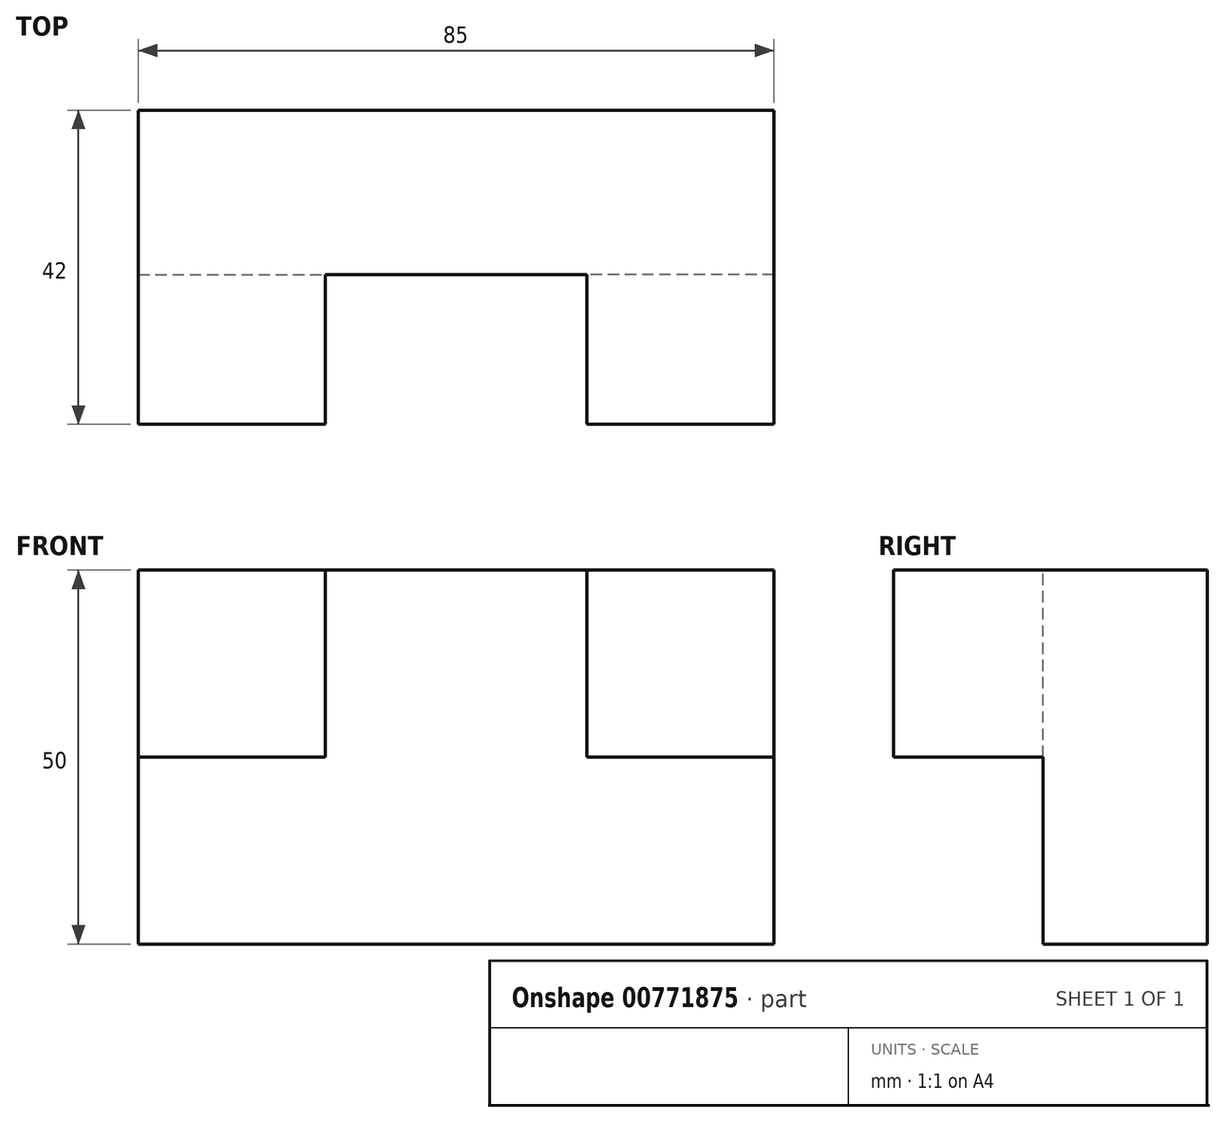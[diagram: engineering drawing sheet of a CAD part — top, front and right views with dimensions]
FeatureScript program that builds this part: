
annotation { "Feature Type Name" : "Feature", "Feature Type Description" : "" }
export const myFeature = defineFeature(function(context is Context, id is Id, definition is map)
    precondition{}
    {
        {
            var Q0;
            Q0=qCreatedBy(makeId("Front.planeOp"),FACE);
            var sketch = newSketch(context, id + "F0", { "sketchPlane" : qUnion([Q0])});
            skLineSegment(sketch, "E0", {"start": v(0, 0) * mm, "end": v(0, 50) * mm});
            skLineSegment(sketch, "E1", {"start": v(0, 50) * mm, "end": v(85, 50) * mm});
            skLineSegment(sketch, "E2", {"start": v(85, 50) * mm, "end": v(85, 0) * mm});
            skLineSegment(sketch, "E3", {"start": v(85, 0) * mm, "end": v(0, 0) * mm});
            skLineSegment(sketch, "E4", {"start": v(0, 25) * mm, "end": v(25, 25) * mm});
            skLineSegment(sketch, "E5", {"start": v(25, 25) * mm, "end": v(25, 50) * mm});
            skLineSegment(sketch, "E6", {"start": v(85, 25) * mm, "end": v(60, 25) * mm});
            skLineSegment(sketch, "E7", {"start": v(60, 25) * mm, "end": v(60, 50) * mm});
            skSolve(sketch);
        }
        {
            var Q0;
            {var subQ0=sQuery(id+"F0.wireOp",EDGE,"E3");Q0=makeQuery(id+"F0.imprint","IMPRINT",FACE,{"disambiguationData":[TD([[makeQuery(id+"F0.imprint","IMPRINT",EDGE,{"derivedFrom":subQ0}),-1.0]])]});}
            extrude(context, id + "F1", {"entities" : qUnion([Q0]), "depth" : 22 * mm, "offsetDistance" : 25 * mm});
        }
        {
            var Q0;
            {var subQ3=sQuery(id+"F0.wireOp",EDGE,"E4");Q0=makeQuery(id+"F0.imprint","IMPRINT",FACE,{"disambiguationData":[TD([[makeQuery(id+"F0.imprint","IMPRINT",EDGE,{"derivedFrom":subQ3}),1.0]])]});}
            var Q1;
            {var subQ4=sQuery(id+"F0.wireOp",EDGE,"E6");Q1=makeQuery(id+"F0.imprint","IMPRINT",FACE,{"disambiguationData":[TD([[makeQuery(id+"F0.imprint","IMPRINT",EDGE,{"derivedFrom":subQ4}),-1.0]])]});}
            extrude(context, id + "F2", {"entities" : qUnion([Q0, Q1]), "operationType" : NewBodyOperationType.ADD, "depth" : 42 * mm, "offsetDistance" : 25 * mm});
        }
    });
